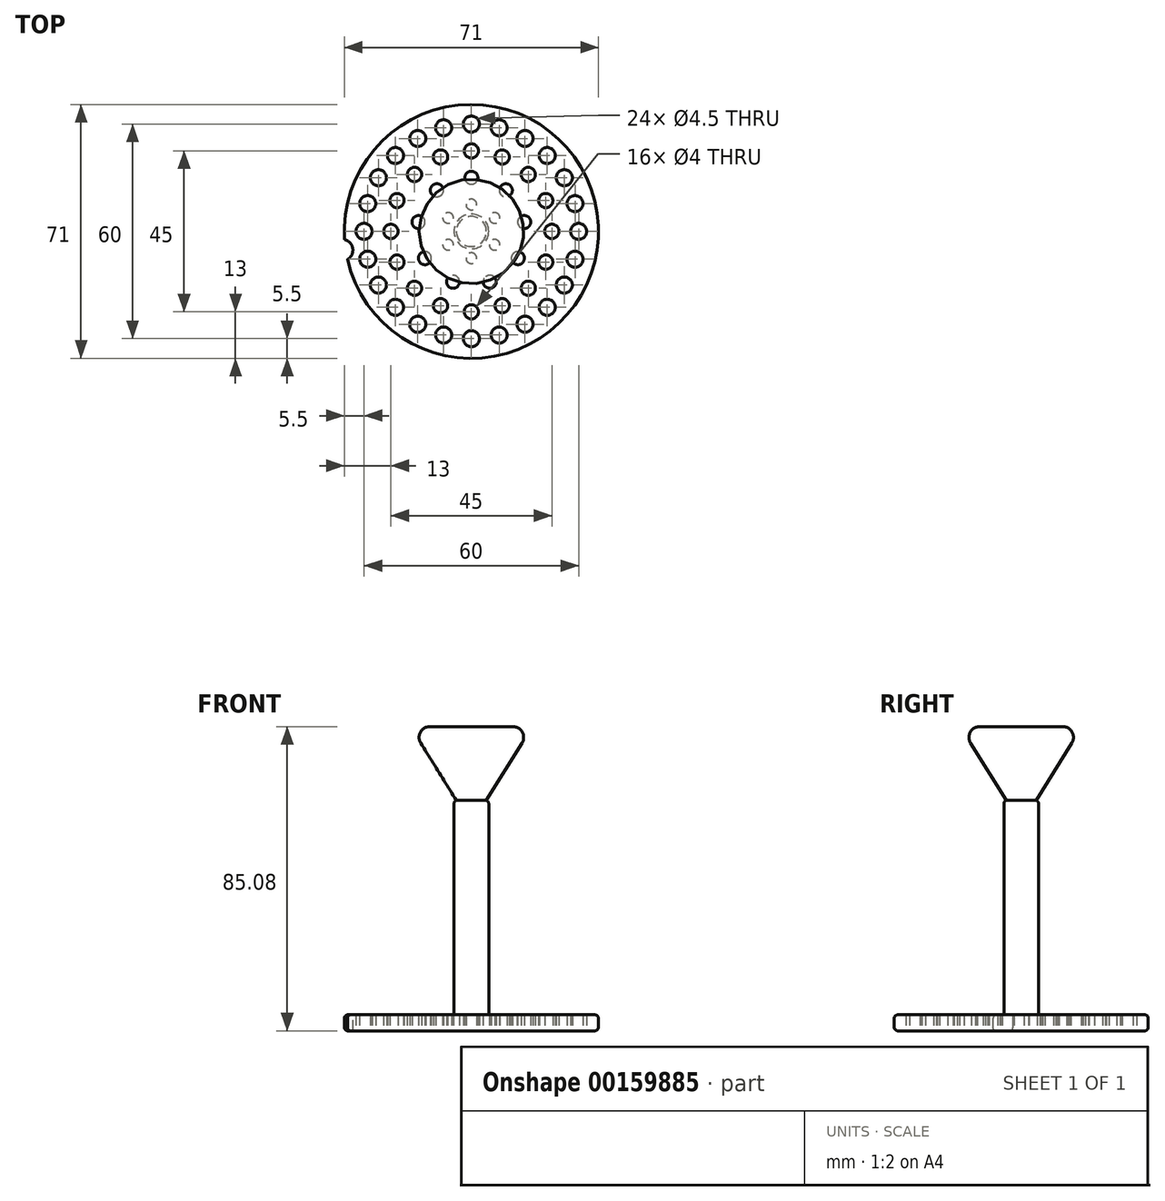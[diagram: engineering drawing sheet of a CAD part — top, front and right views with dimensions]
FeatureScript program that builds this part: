
annotation { "Feature Type Name" : "Feature", "Feature Type Description" : "" }
export const myFeature = defineFeature(function(context is Context, id is Id, definition is map)
    precondition{}
    {
        {
            var Q0;
            Q0=qCreatedBy(makeId("Top.planeOp"),FACE);
            var sketch = newSketch(context, id + "F0", { "sketchPlane" : qUnion([Q0])});
            skCircle(sketch, "E0", {"center": v(0, 0) * mm, "radius": 35.5 * mm});
            skSolve(sketch);
        }
        {
            var Q0;
            Q0=makeQuery(id+"F0.imprint","IMPRINT",FACE,{"disambiguationData":[TD([[makeQuery(id+"F0.imprint","IMPRINT",EDGE,{"derivedFrom":sQuery(id+"F0.wireOp",EDGE,"E0")}),1.0]])]});
            var sketch = newSketch(context, id + "F1", { "sketchPlane" : qUnion([Q0])});
            skCircle(sketch, "E1", {"center": v(0, 0) * mm, "radius": 7.5 * mm, "construction": true});
            skCircle(sketch, "E2", {"center": v(0, 7.5) * mm, "radius": 1.5 * mm});
            skCircle(sketch, "E3.1.1", {"center": v(-6.5, 3.75) * mm, "radius": 1.5 * mm});
            skCircle(sketch, "E3.2.1", {"center": v(-6.5, -3.75) * mm, "radius": 1.5 * mm});
            skCircle(sketch, "E3.3.1", {"center": v(0, -7.5) * mm, "radius": 1.5 * mm});
            skCircle(sketch, "E3.4.1", {"center": v(6.5, -3.75) * mm, "radius": 1.5 * mm});
            skCircle(sketch, "E3.5.1", {"center": v(6.5, 3.75) * mm, "radius": 1.5 * mm});
            skSolve(sketch);
        }
        {
            var Q0;
            Q0=makeQuery(id+"F0.imprint","IMPRINT",FACE,{"disambiguationData":[TD([[makeQuery(id+"F0.imprint","IMPRINT",EDGE,{"derivedFrom":sQuery(id+"F0.wireOp",EDGE,"E0")}),1.0]])]});
            var sketch = newSketch(context, id + "F2", { "sketchPlane" : qUnion([Q0])});
            skCircle(sketch, "E4", {"center": v(0, 0) * mm, "radius": 15 * mm, "construction": true});
            skCircle(sketch, "E5", {"center": v(0, 15) * mm, "radius": 1.83 * mm});
            skCircle(sketch, "E6.1.0", {"center": v(-9.64, 11.5) * mm, "radius": 1.83 * mm});
            skCircle(sketch, "E6.2.0", {"center": v(-14.77, 2.6) * mm, "radius": 1.83 * mm});
            skCircle(sketch, "E6.3.0", {"center": v(-13, -7.5) * mm, "radius": 1.83 * mm});
            skCircle(sketch, "E6.4.0", {"center": v(-5.13, -14.1) * mm, "radius": 1.83 * mm});
            skCircle(sketch, "E6.5.0", {"center": v(5.13, -14.1) * mm, "radius": 1.83 * mm});
            skCircle(sketch, "E6.6.0", {"center": v(13, -7.5) * mm, "radius": 1.83 * mm});
            skCircle(sketch, "E6.7.0", {"center": v(14.77, 2.6) * mm, "radius": 1.83 * mm});
            skCircle(sketch, "E6.8.0", {"center": v(9.64, 11.5) * mm, "radius": 1.83 * mm});
            skSolve(sketch);
        }
        {
            var Q0;
            Q0=makeQuery(id+"F0.imprint","IMPRINT",FACE,{"disambiguationData":[TD([[makeQuery(id+"F0.imprint","IMPRINT",EDGE,{"derivedFrom":sQuery(id+"F0.wireOp",EDGE,"E0")}),1.0]])]});
            var sketch = newSketch(context, id + "F3", { "sketchPlane" : qUnion([Q0])});
            skCircle(sketch, "E7", {"center": v(0, 0) * mm, "radius": 22.5 * mm, "construction": true});
            skCircle(sketch, "E8", {"center": v(0, 22.5) * mm, "radius": 2 * mm});
            skCircle(sketch, "E9.1.0", {"center": v(-8.61, 20.79) * mm, "radius": 2 * mm});
            skCircle(sketch, "E9.2.0", {"center": v(-15.9, 15.9) * mm, "radius": 2 * mm});
            skCircle(sketch, "E9.3.0", {"center": v(-20.79, 8.61) * mm, "radius": 2 * mm});
            skCircle(sketch, "E9.4.0", {"center": v(-22.5, 0) * mm, "radius": 2 * mm});
            skCircle(sketch, "E9.5.0", {"center": v(-20.79, -8.61) * mm, "radius": 2 * mm});
            skCircle(sketch, "E9.6.0", {"center": v(-15.9, -15.9) * mm, "radius": 2 * mm});
            skCircle(sketch, "E9.7.0", {"center": v(-8.61, -20.79) * mm, "radius": 2 * mm});
            skCircle(sketch, "E9.8.0", {"center": v(0, -22.5) * mm, "radius": 2 * mm});
            skCircle(sketch, "E9.9.0", {"center": v(8.61, -20.79) * mm, "radius": 2 * mm});
            skCircle(sketch, "E9.10.0", {"center": v(15.9, -15.9) * mm, "radius": 2 * mm});
            skCircle(sketch, "E9.11.0", {"center": v(20.79, -8.61) * mm, "radius": 2 * mm});
            skCircle(sketch, "E9.12.0", {"center": v(22.5, 0) * mm, "radius": 2 * mm});
            skCircle(sketch, "E9.13.0", {"center": v(20.79, 8.61) * mm, "radius": 2 * mm});
            skCircle(sketch, "E9.14.0", {"center": v(15.9, 15.9) * mm, "radius": 2 * mm});
            skCircle(sketch, "E9.15.0", {"center": v(8.61, 20.79) * mm, "radius": 2 * mm});
            skSolve(sketch);
        }
        {
            var Q0;
            Q0=makeQuery(id+"F0.imprint","IMPRINT",FACE,{"disambiguationData":[TD([[makeQuery(id+"F0.imprint","IMPRINT",EDGE,{"derivedFrom":sQuery(id+"F0.wireOp",EDGE,"E0")}),1.0]])]});
            var sketch = newSketch(context, id + "F4", { "sketchPlane" : qUnion([Q0])});
            skCircle(sketch, "E10", {"center": v(0, 0) * mm, "radius": 30 * mm, "construction": true});
            skCircle(sketch, "E11", {"center": v(0, 30) * mm, "radius": 2.25 * mm});
            skCircle(sketch, "E12.1.0", {"center": v(-7.76, 28.98) * mm, "radius": 2.25 * mm});
            skCircle(sketch, "E12.2.0", {"center": v(-15, 25.98) * mm, "radius": 2.25 * mm});
            skCircle(sketch, "E13.1.3.0", {"center": v(-21.21, 21.21) * mm, "radius": 2.25 * mm});
            skCircle(sketch, "E13.1.4.0", {"center": v(-25.98, 15) * mm, "radius": 2.25 * mm});
            skCircle(sketch, "E13.1.5.0", {"center": v(-28.98, 7.76) * mm, "radius": 2.25 * mm});
            skCircle(sketch, "E13.1.6.0", {"center": v(-30, 0) * mm, "radius": 2.25 * mm});
            skCircle(sketch, "E13.1.7.0", {"center": v(-28.98, -7.76) * mm, "radius": 2.25 * mm});
            skCircle(sketch, "E13.1.8.0", {"center": v(-25.98, -15) * mm, "radius": 2.25 * mm});
            skCircle(sketch, "E13.1.9.0", {"center": v(-21.21, -21.21) * mm, "radius": 2.25 * mm});
            skCircle(sketch, "E13.1.10.0", {"center": v(-15, -25.98) * mm, "radius": 2.25 * mm});
            skCircle(sketch, "E13.1.11.0", {"center": v(-7.76, -28.98) * mm, "radius": 2.25 * mm});
            skCircle(sketch, "E13.1.12.0", {"center": v(0, -30) * mm, "radius": 2.25 * mm});
            skCircle(sketch, "E13.1.13.0", {"center": v(7.76, -28.98) * mm, "radius": 2.25 * mm});
            skCircle(sketch, "E13.1.14.0", {"center": v(15, -25.98) * mm, "radius": 2.25 * mm});
            skCircle(sketch, "E13.1.15.0", {"center": v(21.21, -21.21) * mm, "radius": 2.25 * mm});
            skCircle(sketch, "E13.1.16.0", {"center": v(25.98, -15) * mm, "radius": 2.25 * mm});
            skCircle(sketch, "E13.1.17.0", {"center": v(28.98, -7.76) * mm, "radius": 2.25 * mm});
            skCircle(sketch, "E13.1.18.0", {"center": v(30, 0) * mm, "radius": 2.25 * mm});
            skCircle(sketch, "E13.1.19.0", {"center": v(28.98, 7.76) * mm, "radius": 2.25 * mm});
            skCircle(sketch, "E13.1.20.0", {"center": v(25.98, 15) * mm, "radius": 2.25 * mm});
            skCircle(sketch, "E13.1.21.0", {"center": v(21.21, 21.21) * mm, "radius": 2.25 * mm});
            skCircle(sketch, "E13.1.22.0", {"center": v(15, 25.98) * mm, "radius": 2.25 * mm});
            skCircle(sketch, "E13.1.23.0", {"center": v(7.76, 28.98) * mm, "radius": 2.25 * mm});
            skSolve(sketch);
        }
        {
            var Q0;
            Q0=qSketchRegion(id+"F4",true);
            extrude(context, id + "F5", {"entities" : qUnion([Q0]), "depth" : 5 * mm});
        }
        {
            var Q0;
            Q0=qSketchRegion(id+"F3",true);
            extrude(context, id + "F6", {"entities" : qUnion([Q0]), "depth" : 5 * mm});
        }
        {
            var Q0;
            Q0=qSketchRegion(id+"F2",true);
            extrude(context, id + "F7", {"entities" : qUnion([Q0]), "depth" : 5 * mm});
        }
        {
            var Q0;
            Q0=qSketchRegion(id+"F1",true);
            extrude(context, id + "F8", {"entities" : qUnion([Q0]), "depth" : 5 * mm});
        }
        {
            var Q0;
            Q0=qSketchRegion(id+"F0",true);
            extrude(context, id + "F9", {"entities" : qUnion([Q0]), "depth" : 4.5 * mm});
        }
        {
            var Q0;
            Q0=makeQuery(id+"F5.opExtrude","SWEPT_BODY",BODY,{"disambiguationData":[OSD([sQuery(id+"F4.wireOp",EDGE,"E11")])]});
            var Q1;
            Q1=makeQuery(id+"F5.opExtrude","SWEPT_BODY",BODY,{"disambiguationData":[OSD([sQuery(id+"F4.wireOp",EDGE,"E13.1.3.0")])]});
            var Q2;
            Q2=makeQuery(id+"F5.opExtrude","SWEPT_BODY",BODY,{"disambiguationData":[OSD([sQuery(id+"F4.wireOp",EDGE,"E13.1.7.0")])]});
            var Q3;
            Q3=makeQuery(id+"F5.opExtrude","SWEPT_BODY",BODY,{"disambiguationData":[OSD([sQuery(id+"F4.wireOp",EDGE,"E12.1.0")])]});
            var Q4;
            Q4=makeQuery(id+"F5.opExtrude","SWEPT_BODY",BODY,{"disambiguationData":[OSD([sQuery(id+"F4.wireOp",EDGE,"E12.2.0")])]});
            var Q5;
            Q5=makeQuery(id+"F5.opExtrude","SWEPT_BODY",BODY,{"disambiguationData":[OSD([sQuery(id+"F4.wireOp",EDGE,"E13.1.4.0")])]});
            var Q6;
            Q6=makeQuery(id+"F5.opExtrude","SWEPT_BODY",BODY,{"disambiguationData":[OSD([sQuery(id+"F4.wireOp",EDGE,"E13.1.5.0")])]});
            var Q7;
            Q7=makeQuery(id+"F5.opExtrude","SWEPT_BODY",BODY,{"disambiguationData":[OSD([sQuery(id+"F4.wireOp",EDGE,"E13.1.6.0")])]});
            var Q8;
            Q8=makeQuery(id+"F5.opExtrude","SWEPT_BODY",BODY,{"disambiguationData":[OSD([sQuery(id+"F4.wireOp",EDGE,"E13.1.8.0")])]});
            var Q9;
            Q9=makeQuery(id+"F5.opExtrude","SWEPT_BODY",BODY,{"disambiguationData":[OSD([sQuery(id+"F4.wireOp",EDGE,"E13.1.9.0")])]});
            var Q10;
            Q10=makeQuery(id+"F5.opExtrude","SWEPT_BODY",BODY,{"disambiguationData":[OSD([sQuery(id+"F4.wireOp",EDGE,"E13.1.10.0")])]});
            var Q11;
            Q11=makeQuery(id+"F5.opExtrude","SWEPT_BODY",BODY,{"disambiguationData":[OSD([sQuery(id+"F4.wireOp",EDGE,"E13.1.11.0")])]});
            var Q12;
            Q12=makeQuery(id+"F5.opExtrude","SWEPT_BODY",BODY,{"disambiguationData":[OSD([sQuery(id+"F4.wireOp",EDGE,"E13.1.12.0")])]});
            var Q13;
            Q13=makeQuery(id+"F5.opExtrude","SWEPT_BODY",BODY,{"disambiguationData":[OSD([sQuery(id+"F4.wireOp",EDGE,"E13.1.13.0")])]});
            var Q14;
            Q14=makeQuery(id+"F5.opExtrude","SWEPT_BODY",BODY,{"disambiguationData":[OSD([sQuery(id+"F4.wireOp",EDGE,"E13.1.14.0")])]});
            var Q15;
            Q15=makeQuery(id+"F5.opExtrude","SWEPT_BODY",BODY,{"disambiguationData":[OSD([sQuery(id+"F4.wireOp",EDGE,"E13.1.15.0")])]});
            var Q16;
            Q16=makeQuery(id+"F5.opExtrude","SWEPT_BODY",BODY,{"disambiguationData":[OSD([sQuery(id+"F4.wireOp",EDGE,"E13.1.16.0")])]});
            var Q17;
            Q17=makeQuery(id+"F5.opExtrude","SWEPT_BODY",BODY,{"disambiguationData":[OSD([sQuery(id+"F4.wireOp",EDGE,"E13.1.17.0")])]});
            var Q18;
            Q18=makeQuery(id+"F5.opExtrude","SWEPT_BODY",BODY,{"disambiguationData":[OSD([sQuery(id+"F4.wireOp",EDGE,"E13.1.18.0")])]});
            var Q19;
            Q19=makeQuery(id+"F5.opExtrude","SWEPT_BODY",BODY,{"disambiguationData":[OSD([sQuery(id+"F4.wireOp",EDGE,"E13.1.19.0")])]});
            var Q20;
            Q20=makeQuery(id+"F5.opExtrude","SWEPT_BODY",BODY,{"disambiguationData":[OSD([sQuery(id+"F4.wireOp",EDGE,"E13.1.20.0")])]});
            var Q21;
            Q21=makeQuery(id+"F5.opExtrude","SWEPT_BODY",BODY,{"disambiguationData":[OSD([sQuery(id+"F4.wireOp",EDGE,"E13.1.21.0")])]});
            var Q22;
            Q22=makeQuery(id+"F5.opExtrude","SWEPT_BODY",BODY,{"disambiguationData":[OSD([sQuery(id+"F4.wireOp",EDGE,"E13.1.22.0")])]});
            var Q23;
            Q23=makeQuery(id+"F5.opExtrude","SWEPT_BODY",BODY,{"disambiguationData":[OSD([sQuery(id+"F4.wireOp",EDGE,"E13.1.23.0")])]});
            var Q24;
            Q24=makeQuery(id+"F6.opExtrude","SWEPT_BODY",BODY,{"disambiguationData":[OSD([sQuery(id+"F3.wireOp",EDGE,"E9.15.0")])]});
            var Q25;
            Q25=makeQuery(id+"F6.opExtrude","SWEPT_BODY",BODY,{"disambiguationData":[OSD([sQuery(id+"F3.wireOp",EDGE,"E8")])]});
            var Q26;
            Q26=makeQuery(id+"F6.opExtrude","SWEPT_BODY",BODY,{"disambiguationData":[OSD([sQuery(id+"F3.wireOp",EDGE,"E9.1.0")])]});
            var Q27;
            Q27=makeQuery(id+"F6.opExtrude","SWEPT_BODY",BODY,{"disambiguationData":[OSD([sQuery(id+"F3.wireOp",EDGE,"E9.2.0")])]});
            var Q28;
            Q28=makeQuery(id+"F6.opExtrude","SWEPT_BODY",BODY,{"disambiguationData":[OSD([sQuery(id+"F3.wireOp",EDGE,"E9.3.0")])]});
            var Q29;
            Q29=makeQuery(id+"F6.opExtrude","SWEPT_BODY",BODY,{"disambiguationData":[OSD([sQuery(id+"F3.wireOp",EDGE,"E9.4.0")])]});
            var Q30;
            Q30=makeQuery(id+"F6.opExtrude","SWEPT_BODY",BODY,{"disambiguationData":[OSD([sQuery(id+"F3.wireOp",EDGE,"E9.5.0")])]});
            var Q31;
            Q31=makeQuery(id+"F6.opExtrude","SWEPT_BODY",BODY,{"disambiguationData":[OSD([sQuery(id+"F3.wireOp",EDGE,"E9.6.0")])]});
            var Q32;
            Q32=makeQuery(id+"F6.opExtrude","SWEPT_BODY",BODY,{"disambiguationData":[OSD([sQuery(id+"F3.wireOp",EDGE,"E9.7.0")])]});
            var Q33;
            Q33=makeQuery(id+"F6.opExtrude","SWEPT_BODY",BODY,{"disambiguationData":[OSD([sQuery(id+"F3.wireOp",EDGE,"E9.8.0")])]});
            var Q34;
            Q34=makeQuery(id+"F6.opExtrude","SWEPT_BODY",BODY,{"disambiguationData":[OSD([sQuery(id+"F3.wireOp",EDGE,"E9.9.0")])]});
            var Q35;
            Q35=makeQuery(id+"F6.opExtrude","SWEPT_BODY",BODY,{"disambiguationData":[OSD([sQuery(id+"F3.wireOp",EDGE,"E9.10.0")])]});
            var Q36;
            Q36=makeQuery(id+"F6.opExtrude","SWEPT_BODY",BODY,{"disambiguationData":[OSD([sQuery(id+"F3.wireOp",EDGE,"E9.11.0")])]});
            var Q37;
            Q37=makeQuery(id+"F6.opExtrude","SWEPT_BODY",BODY,{"disambiguationData":[OSD([sQuery(id+"F3.wireOp",EDGE,"E9.12.0")])]});
            var Q38;
            Q38=makeQuery(id+"F6.opExtrude","SWEPT_BODY",BODY,{"disambiguationData":[OSD([sQuery(id+"F3.wireOp",EDGE,"E9.13.0")])]});
            var Q39;
            Q39=makeQuery(id+"F6.opExtrude","SWEPT_BODY",BODY,{"disambiguationData":[OSD([sQuery(id+"F3.wireOp",EDGE,"E9.14.0")])]});
            var Q40;
            Q40=makeQuery(id+"F7.opExtrude","SWEPT_BODY",BODY,{"disambiguationData":[OSD([sQuery(id+"F2.wireOp",EDGE,"E6.8.0")])]});
            var Q41;
            Q41=makeQuery(id+"F7.opExtrude","SWEPT_BODY",BODY,{"disambiguationData":[OSD([sQuery(id+"F2.wireOp",EDGE,"E6.7.0")])]});
            var Q42;
            Q42=makeQuery(id+"F7.opExtrude","SWEPT_BODY",BODY,{"disambiguationData":[OSD([sQuery(id+"F2.wireOp",EDGE,"E6.6.0")])]});
            var Q43;
            Q43=makeQuery(id+"F7.opExtrude","SWEPT_BODY",BODY,{"disambiguationData":[OSD([sQuery(id+"F2.wireOp",EDGE,"E6.5.0")])]});
            var Q44;
            Q44=makeQuery(id+"F7.opExtrude","SWEPT_BODY",BODY,{"disambiguationData":[OSD([sQuery(id+"F2.wireOp",EDGE,"E6.4.0")])]});
            var Q45;
            Q45=makeQuery(id+"F7.opExtrude","SWEPT_BODY",BODY,{"disambiguationData":[OSD([sQuery(id+"F2.wireOp",EDGE,"E6.3.0")])]});
            var Q46;
            Q46=makeQuery(id+"F7.opExtrude","SWEPT_BODY",BODY,{"disambiguationData":[OSD([sQuery(id+"F2.wireOp",EDGE,"E6.2.0")])]});
            var Q47;
            Q47=makeQuery(id+"F7.opExtrude","SWEPT_BODY",BODY,{"disambiguationData":[OSD([sQuery(id+"F2.wireOp",EDGE,"E6.1.0")])]});
            var Q48;
            Q48=makeQuery(id+"F7.opExtrude","SWEPT_BODY",BODY,{"disambiguationData":[OSD([sQuery(id+"F2.wireOp",EDGE,"E5")])]});
            var Q49;
            Q49=makeQuery(id+"F8.opExtrude","SWEPT_BODY",BODY,{"disambiguationData":[OSD([sQuery(id+"F1.wireOp",EDGE,"E2")])]});
            var Q50;
            Q50=makeQuery(id+"F8.opExtrude","SWEPT_BODY",BODY,{"disambiguationData":[OSD([sQuery(id+"F1.wireOp",EDGE,"E3.5.1")])]});
            var Q51;
            Q51=makeQuery(id+"F8.opExtrude","SWEPT_BODY",BODY,{"disambiguationData":[OSD([sQuery(id+"F1.wireOp",EDGE,"E3.4.1")])]});
            var Q52;
            Q52=makeQuery(id+"F8.opExtrude","SWEPT_BODY",BODY,{"disambiguationData":[OSD([sQuery(id+"F1.wireOp",EDGE,"E3.3.1")])]});
            var Q53;
            Q53=makeQuery(id+"F8.opExtrude","SWEPT_BODY",BODY,{"disambiguationData":[OSD([sQuery(id+"F1.wireOp",EDGE,"E3.2.1")])]});
            var Q54;
            Q54=makeQuery(id+"F8.opExtrude","SWEPT_BODY",BODY,{"disambiguationData":[OSD([sQuery(id+"F1.wireOp",EDGE,"E3.1.1")])]});
            var Q55;
            Q55=makeQuery(id+"F9.opExtrude","SWEPT_BODY",BODY,{"disambiguationData":[OSD([sQuery(id+"F0.wireOp",EDGE,"E0")])]});
            booleanBodies(context, id + "F10", {"operationType" : BooleanOperationType.SUBTRACTION, "tools" : qUnion([Q0, Q1, Q2, Q3, Q4, Q5, Q6, Q7, Q8, Q9, Q10, Q11, Q12, Q13, Q14, Q15, Q16, Q17, Q18, Q19, Q20, Q21, Q22, Q23, Q24, Q25, Q26, Q27, Q28, Q29, Q30, Q31, Q32, Q33, Q34, Q35, Q36, Q37, Q38, Q39, Q40, Q41, Q42, Q43, Q44, Q45, Q46, Q47, Q48, Q49, Q50, Q51, Q52, Q53, Q54]), "targets" : qUnion([Q55])});
        }
        {
            var Q0;
            Q0=makeQuery(id+"F9.opExtrude","CAP_EDGE",EDGE,{"disambiguationData":[OSD([sQuery(id+"F0.wireOp",EDGE,"E0")])],"isStart":true});
            var Q1;
            Q1=makeQuery(id+"F9.opExtrude","CAP_EDGE",EDGE,{"disambiguationData":[OSD([sQuery(id+"F0.wireOp",EDGE,"E0")])],"isStart":false});
            fillet(context, id + "F11", {"entities" : qUnion([Q0, Q1]), "radius" : 1 * mm, "tangentPropagation" : true, "allowEdgeOverflow" : false});
        }
        {
            var Q0;
            Q0=makeQuery(id+"F9.opExtrude","CAP_FACE",FACE,{"disambiguationData":[OSD([sQuery(id+"F0.wireOp",EDGE,"E0")])],"isStart":false});
            var sketch = newSketch(context, id + "F12", { "sketchPlane" : qUnion([Q0])});
            skCircle(sketch, "E14", {"center": v(0, 0) * mm, "radius": 4.85 * mm});
            skSolve(sketch);
        }
        {
            var Q0;
            Q0=makeQuery(id+"F12.imprint","IMPRINT",FACE,{"disambiguationData":[TD([[makeQuery(id+"F12.imprint","IMPRINT",EDGE,{"derivedFrom":sQuery(id+"F12.wireOp",EDGE,"E14")}),1.0]])]});
            extrude(context, id + "F13", {"entities" : qUnion([Q0]), "operationType" : NewBodyOperationType.ADD, "depth" : 60 * mm, "offsetDistance" : 25 * mm});
        }
        {
            var Q0;
            Q0=makeQuery(id+"F13.opExtrude","CAP_EDGE",EDGE,{"disambiguationData":[OSD([sQuery(id+"F12.wireOp",EDGE,"E14")])],"isStart":false});
            fillet(context, id + "F14", {"entities" : qUnion([Q0]), "radius" : 1 * mm, "tangentPropagation" : true, "allowEdgeOverflow" : false});
        }
        {
            var Q0;
            Q0=makeQuery(id+"F9.opExtrude","CAP_FACE",FACE,{"disambiguationData":[OSD([sQuery(id+"F0.wireOp",EDGE,"E0")])],"isStart":false});
            var sketch = newSketch(context, id + "F15", { "sketchPlane" : qUnion([Q0])});
            skCircle(sketch, "E15", {"center": v(0, 0) * mm, "radius": 36.5 * mm, "construction": true});
            skCircle(sketch, "E16", {"center": v(-36.12, -5.23) * mm, "radius": 3 * mm});
            skSolve(sketch);
        }
        {
            var Q0;
            Q0=makeQuery(id+"F15.imprint","IMPRINT",FACE,{"disambiguationData":[TD([[makeQuery(id+"F15.imprint","IMPRINT",EDGE,{"derivedFrom":sQuery(id+"F15.wireOp",EDGE,"E16")}),1.0]])]});
            extrude(context, id + "F16", {"entities" : qUnion([Q0]), "operationType" : NewBodyOperationType.REMOVE, "oppositeDirection" : true, "depth" : 25 * mm});
        }
        {
            var Q0;
            Q0=makeQuery(id+"F13.opExtrude","CAP_FACE",FACE,{"disambiguationData":[OSD([sQuery(id+"F12.wireOp",EDGE,"E14")])],"isStart":false});
            var sketch = newSketch(context, id + "F17", { "sketchPlane" : qUnion([Q0])});
            skCircle(sketch, "E17", {"center": v(0, 0) * mm, "radius": 3.98 * mm});
            skSolve(sketch);
        }
        {
            var Q0;
            Q0=qSketchRegion(id+"F17",true);
            extrude(context, id + "F18", {"entities" : qUnion([Q0]), "operationType" : NewBodyOperationType.ADD, "depth" : 2 * mm, "offsetDistance" : 25 * mm});
        }
        {
            var Q0;
            Q0=qCreatedBy(makeId("Front.planeOp"),FACE);
            var sketch = newSketch(context, id + "F19", { "sketchPlane" : qUnion([Q0])});
            skLineSegment(sketch, "E18", {"start": v(0, 64.6) * mm, "end": v(0, 85.08) * mm, "construction": true});
            skLineSegment(sketch, "E19", {"start": v(0, 85.08) * mm, "end": v(-17, 85.08) * mm});
            skLineSegment(sketch, "E20", {"start": v(-17, 85.08) * mm, "end": v(-4.06, 64.2) * mm});
            skLineSegment(sketch, "E21", {"start": v(-4.06, 64.2) * mm, "end": v(0, 64.2) * mm});
            skLineSegment(sketch, "E22", {"start": v(0, 64.2) * mm, "end": v(0, 85.08) * mm});
            skSolve(sketch);
        }
        {
            var Q0;
            Q0=makeQuery(id+"F19.imprint","IMPRINT",FACE,{"disambiguationData":[TD([[makeQuery(id+"F19.imprint","IMPRINT",EDGE,{"derivedFrom":sQuery(id+"F19.wireOp",EDGE,"E19")}),1.0]])]});
            var Q1;
            Q1=sQuery(id+"F19.wireOp",EDGE,"E22");
            revolve(context, id + "F20", {"operationType" : NewBodyOperationType.ADD, "surfaceOperationType" : NewSurfaceOperationType.NEW, "entities" : qUnion([Q0]), "axis" : qUnion([Q1]), "revolveType" : RevolveType.FULL});
        }
        {
            var Q0;
            Q0=makeQuery(id+"F20.opRevolve","SWEPT_EDGE",EDGE,{"disambiguationData":[OSD([sQuery(id+"F19.wireOp",EDGE,"E19"),sQuery(id+"F19.wireOp",EDGE,"E20")])]});
            fillet(context, id + "F21", {"entities" : qUnion([Q0]), "radius" : 3 * mm, "tangentPropagation" : true, "allowEdgeOverflow" : false});
        }
    });
